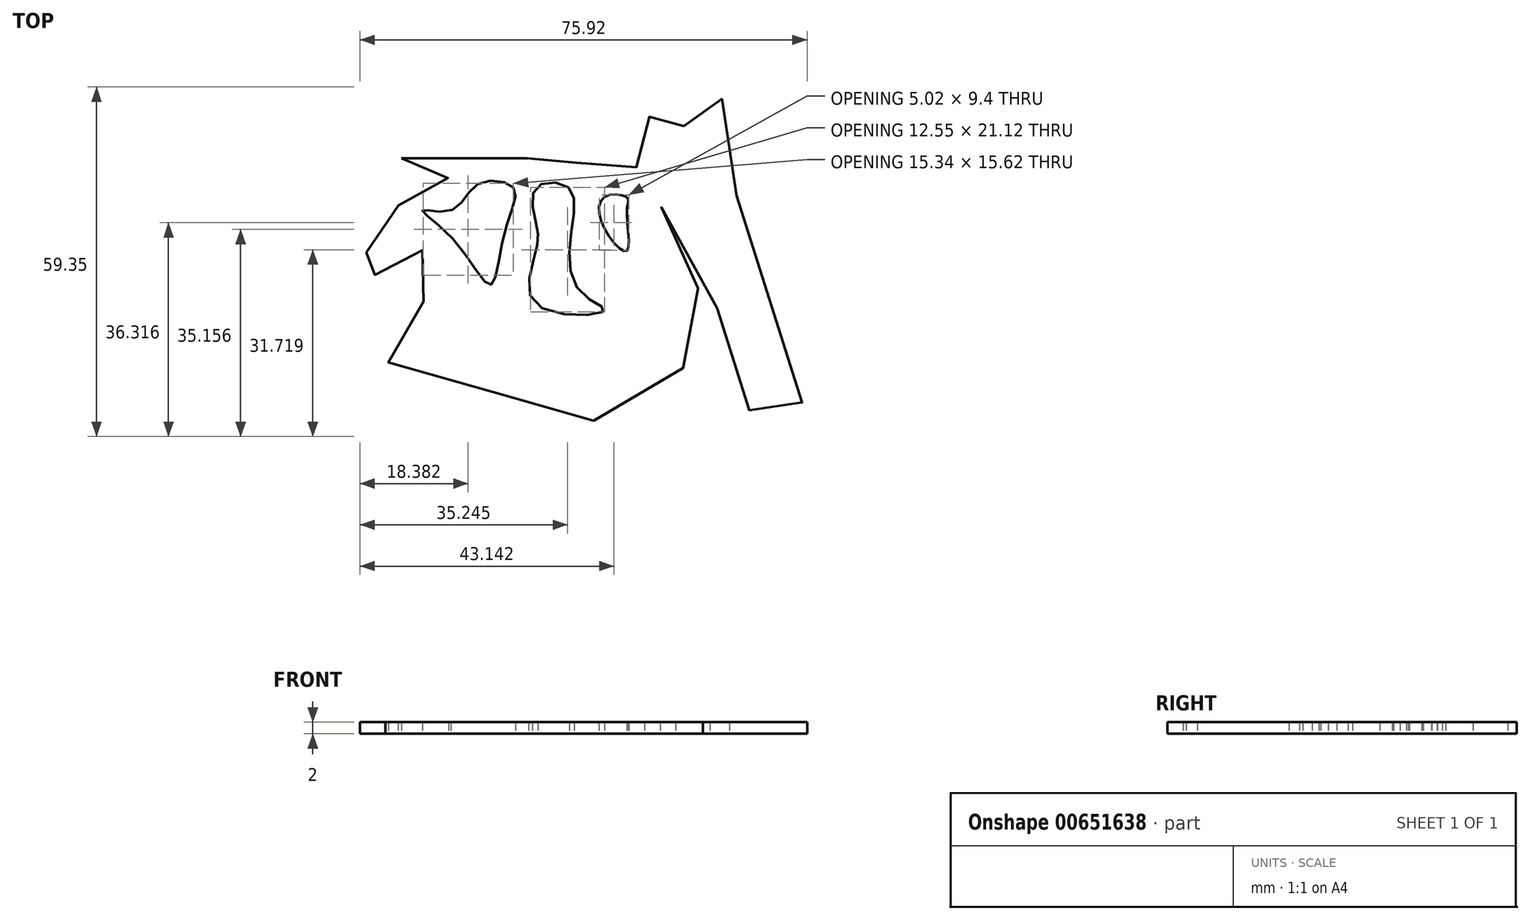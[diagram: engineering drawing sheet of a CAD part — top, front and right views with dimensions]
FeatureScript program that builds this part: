
annotation { "Feature Type Name" : "Feature", "Feature Type Description" : "" }
export const myFeature = defineFeature(function(context is Context, id is Id, definition is map)
    precondition{}
    {
        {
            var Q0;
            Q0=qCreatedBy(makeId("Top.planeOp"),FACE);
            var sketch = newSketch(context, id + "F0", { "sketchPlane" : qUnion([Q0])});
            skFitSpline(sketch, "E0", {"points": [v(-68.44, 47.23) * mm, v(-70.64, 46.13) * mm, v(-64.86, 44.2) * mm, v(-60.45, 43.65) * mm, v(-64.86, 40.62) * mm, v(-67.06, 40.9) * mm, v(-69, 39.52) * mm, v(-68.44, 37.87) * mm, v(-72.85, 34.84) * mm, v(-73.67, 31.54) * mm, v(-75.33, 30.7) * mm, v(-75.05, 28.78) * mm, v(-73.95, 30.7) * mm, v(-73.12, 27.4) * mm, v(-71.2, 33.74) * mm, v(-68.72, 35.94) * mm, v(-61.28, 25.48) * mm, v(-60.18, 22.45) * mm, v(-63.48, 23) * mm, v(-70.1, 20.52) * mm, v(-71.2, 16.66) * mm, v(-69.54, 11.15) * mm, v(-57.98, 9.78) * mm, v(-48.89, 5.1) * mm, v(-39.25, 2.9) * mm, v(-31.26, 3.44) * mm, v(-22.45, 9.5) * mm, v(-18.04, 17.76) * mm, v(-17.49, 26.03) * mm, v(-18.6, 24.65) * mm, v(-23, 31.54) * mm, v(-24.1, 39.25) * mm, v(-21.34, 38.42) * mm, v(-13.9, 16.66) * mm, v(-11.43, 3.17) * mm, v(-7.3, 5.1) * mm, v(0, 0) * mm, v(-7.57, 28.5) * mm, v(-14.46, 49.71) * mm, v(-15.56, 56.87) * mm, v(-12.8, 57.7) * mm, v(-15.01, 59.35) * mm, v(-20.24, 54.12) * mm, v(-20.8, 51.92) * mm, v(-25.2, 57.42) * mm, v(-27.13, 56.87) * mm, v(-21.9, 45.3) * mm, v(-24.65, 45.3) * mm, v(-29.6, 45.3) * mm, v(-30.16, 43.65) * mm, v(-36.77, 45.03) * mm, v(-39.25, 46.68) * mm, v(-41.45, 45.58) * mm, v(-45.58, 45.3) * mm, v(-46.96, 47.23) * mm, v(-49.71, 46.13) * mm, v(-68.44, 47.23) * mm]});
            skFitSpline(sketch, "E1", {"points": [v(-49.44, 42.28) * mm, v(-55.5, 42.83) * mm, v(-59.9, 38.42) * mm, v(-64.86, 38.42) * mm, v(-59.63, 33.46) * mm, v(-53.3, 25.75) * mm, v(-50.81, 35.12) * mm, v(-49.44, 42.28) * mm]});
            skFitSpline(sketch, "E2", {"points": [v(-40.07, 42.28) * mm, v(-45.58, 42.28) * mm, v(-45.58, 36.22) * mm, v(-45.58, 31.54) * mm, v(-45.58, 22.45) * mm, v(-34.01, 21.34) * mm, v(-38.15, 24.65) * mm, v(-39.52, 35.4) * mm, v(-40.07, 42.28) * mm]});
            skFitSpline(sketch, "E3", {"points": [v(-34.01, 40.62) * mm, v(-30.16, 40.62) * mm, v(-30.16, 38.42) * mm, v(-30.16, 31.54) * mm, v(-34.01, 35.4) * mm, v(-34.01, 40.62) * mm]});
            skSolve(sketch);
        }
        {
            var Q0;
            Q0 = qSketchRegion(id + "F0", true);
            extrude(context, id + "F1", {"entities" : qUnion([Q0]), "depth" : 2 * mm, "offsetDistance" : 25 * mm});
        }
    });
